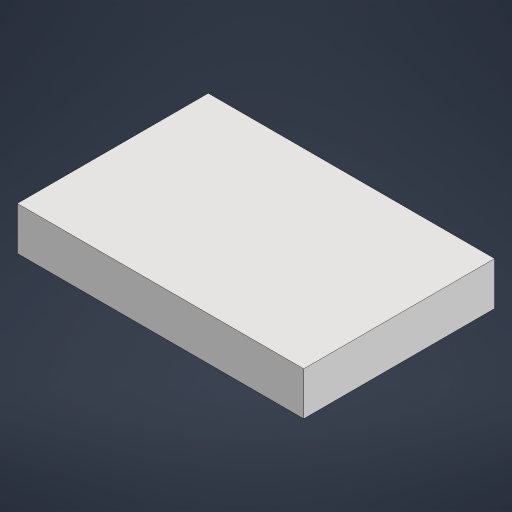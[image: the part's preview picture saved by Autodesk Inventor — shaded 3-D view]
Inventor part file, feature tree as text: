
AUTODESK INVENTOR PART (.ipt)
format: ipt  version: 2023.1 (Build 271208000, 208)  size: 146,432 bytes
history: native  units: in
note: dims shown in document units (in); Inventor stores cm internally (conversion verified against a paired STEP export)
features: extrude x1, sketch x1
ambient origin geometry x8: Origin, YZ Plane, XZ Plane, XY Plane, X Axis, Y Axis, Z Axis, Center Point
bodies: Solid1 (feature_tree)
feature tree (2):
  extrude  "Extrusion1"  Depth=16.0in
  sketch  "Sketch2"  dims[d3=24.0in d4=16.0in d5=3.625in d6=0.0in]
